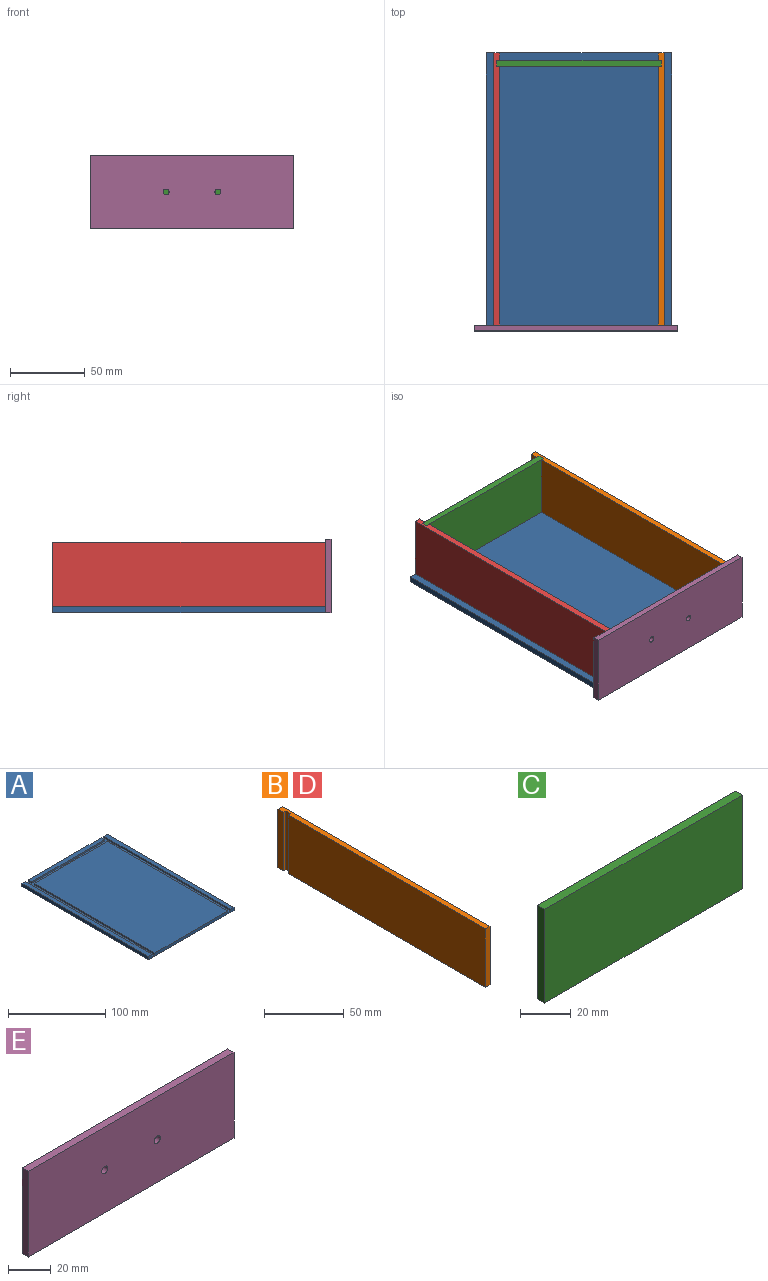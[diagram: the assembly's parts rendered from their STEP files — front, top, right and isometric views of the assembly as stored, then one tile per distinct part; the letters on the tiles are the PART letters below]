
ASSEMBLY  parts=5 mates=4
PART A: 18 faces, bbox 124x184x4 mm
  f0: plane 124x4mm, normal (0,1,0), area 480mm2, adj f2,f3,f4,f6,f7,f8,f9,f13
  f1: plane 175x106mm, normal (0,0,1), area 18550mm2, adj f5,f10,f11,f12
  f2: plane 184x5mm, normal (0,0,1), area 920mm2, adj f0,f5,f6,f13
  f3: plane 184x5mm, normal (0,0,1), area 920mm2, adj f0,f4,f5,f9
  f4: plane 184x4mm, normal (-1,0,0), area 736mm2, adj f0,f3,f5,f8
  f5: plane 124x4mm, normal (0,-1,0), area 480mm2, adj f1,f2,f3,f4,f6,f8,f9,f10
  f6: plane 184x4mm, normal (1,0,0), area 736mm2, adj f0,f2,f5,f8
  f7: plane 106x5mm, normal (0,0,1), area 530mm2, adj f0,f14,f15,f16
  f8: plane 184x124mm, normal (0,0,-1), area 22816mm2, adj f0,f4,f5,f6
  f9: plane 184x2mm, normal (1,0,0), area 368mm2, adj f0,f3,f5,f17
  f10: plane 175x2mm, normal (-1,0,0), area 350mm2, adj f1,f5,f11,f17
  f11: plane 106x2mm, normal (0,1,0), area 212mm2, adj f1,f10,f12,f17
  f12: plane 175x2mm, normal (1,0,0), area 350mm2, adj f1,f5,f11,f17
  f13: plane 184x2mm, normal (-1,0,0), area 368mm2, adj f0,f2,f5,f17
  f14: plane 5x2mm, normal (1,0,0), area 10mm2, adj f0,f7,f15,f17
  f15: plane 106x2mm, normal (0,-1,0), area 212mm2, adj f7,f14,f16,f17
  f16: plane 5x2mm, normal (-1,0,0), area 10mm2, adj f0,f7,f15,f17
  f17: plane 184x114mm, normal (0,0,1), area 1896mm2, adj f0,f5,f9,f10,f11,f12,f13,f14
PART B: 10 faces, bbox 4x184x45 mm
  f0: plane 45x5mm, normal (-1,0,0), area 225mm2, adj f1,f3,f4,f7
  f1: plane 184x4mm, normal (0,0,1), area 728mm2, adj f0,f2,f4,f5,f6,f7,f8,f9
  f2: plane 45x4mm, normal (0,-1,0), area 180mm2, adj f1,f3,f5,f6
  f3: plane 184x4mm, normal (0,0,-1), area 728mm2, adj f0,f2,f4,f5,f6,f7,f8,f9
  f4: plane 45x4mm, normal (0,1,0), area 180mm2, adj f0,f1,f3,f5
  f5: plane 184x45mm, normal (1,0,0), area 8280mm2, adj f1,f2,f3,f4
  f6: plane 175x45mm, normal (-1,0,0), area 7875mm2, adj f1,f2,f3,f8
  f7: plane 45x2mm, normal (0,-1,0), area 90mm2, adj f0,f1,f3,f9
  f8: plane 45x2mm, normal (0,1,0), area 90mm2, adj f1,f3,f6,f9
  f9: plane 45x4mm, normal (-1,0,0), area 180mm2, adj f1,f3,f7,f8
PART C: 6 faces, bbox 110x4x45 mm
  f0: plane 45x4mm, normal (1,0,0), area 180mm2, adj f1,f3,f4,f5
  f1: plane 110x4mm, normal (0,0,1), area 440mm2, adj f0,f2,f4,f5
  f2: plane 45x4mm, normal (-1,0,0), area 180mm2, adj f1,f3,f4,f5
  f3: plane 110x4mm, normal (0,0,-1), area 440mm2, adj f0,f2,f4,f5
  f4: plane 110x45mm, normal (0,-1,0), area 4950mm2, adj f0,f1,f2,f3
  f5: plane 110x45mm, normal (0,1,0), area 4950mm2, adj f0,f1,f2,f3
PART D: same geometry as B
PART E: 20 faces, bbox 136x4x49 mm
  f0: plane 136x4mm, normal (0,0,1), area 544mm2, adj f1,f5,f6,f7
  f1: plane 49x4mm, normal (-1,0,0), area 196mm2, adj f0,f2,f6,f7
  f2: plane 136x4mm, normal (0,0,-1), area 304mm2, adj f1,f5,f6,f7,f10,f11,f19
  f3: cylinder r=2mm len=4mm, axis (0,1,0), area 50.3mm2, adj f6,f7
  f4: cylinder r=2mm len=4mm, axis (0,1,0), area 50.3mm2, adj f6,f7
  f5: plane 49x4mm, normal (1,0,0), area 196mm2, adj f0,f2,f6,f7
  f6: plane 136x49mm, normal (0,-1,0), area 6638.9mm2, adj f0,f1,f2,f3,f4,f5
  f7: plane 136x49mm, normal (0,1,0), area 5830.9mm2, adj f0,f1,f2,f3,f4,f5,f8,f9
  f8: plane 41x2mm, normal (-1,0,0), area 82mm2, adj f7,f9,f18,f19
  f9: plane 2x1mm, normal (0,0,-1), area 2mm2, adj f7,f8,f10,f19
  f10: plane 4x2mm, normal (-1,0,0), area 8mm2, adj f2,f7,f9,f19
  f11: plane 4x2mm, normal (1,0,0), area 8mm2, adj f2,f7,f12,f19
  f12: plane 2x1mm, normal (0,0,-1), area 2mm2, adj f7,f11,f13,f19
  f13: plane 41x2mm, normal (1,0,0), area 82mm2, adj f7,f12,f14,f19
  f14: plane 4x2mm, normal (0,0,-1), area 8mm2, adj f7,f13,f15,f19
  f15: plane 41x2mm, normal (-1,0,0), area 82mm2, adj f7,f14,f16,f19
  f16: plane 110x2mm, normal (0,0,-1), area 220mm2, adj f7,f15,f17,f19
  f17: plane 41x2mm, normal (1,0,0), area 82mm2, adj f7,f16,f18,f19
  f18: plane 4x2mm, normal (0,0,-1), area 8mm2, adj f7,f8,f17,f19
  f19: plane 120x45mm, normal (0,1,0), area 808mm2, adj f2,f8,f9,f10,f11,f12,f13,f14
PLACE A t=(76.81,-75.22,-21.53)mm
PLACE B t=(129.81,-75.22,2.97)mm
PLACE C t=(76.81,11.78,2.97)mm
PLACE D rot(axis=(0,1,0),180deg) t=(23.81,-75.22,2.97)mm
PLACE E t=(74.81,-165.22,2.97)mm
MATE fastened C.f1 <-> B.f1  axis (0,0,-1) through (131.81,7.78,25.47)mm
MATE fastened D.f1 <-> A.f17  axis (0,0,-1) through (19.81,16.78,-19.53)mm
MATE fastened B.f3 <-> A.f17  axis (0,0,1) through (133.81,16.78,-19.53)mm
MATE fastened E.f2 <-> A.f8  axis (0,0,1) through (14.81,-167.22,-21.53)mm
